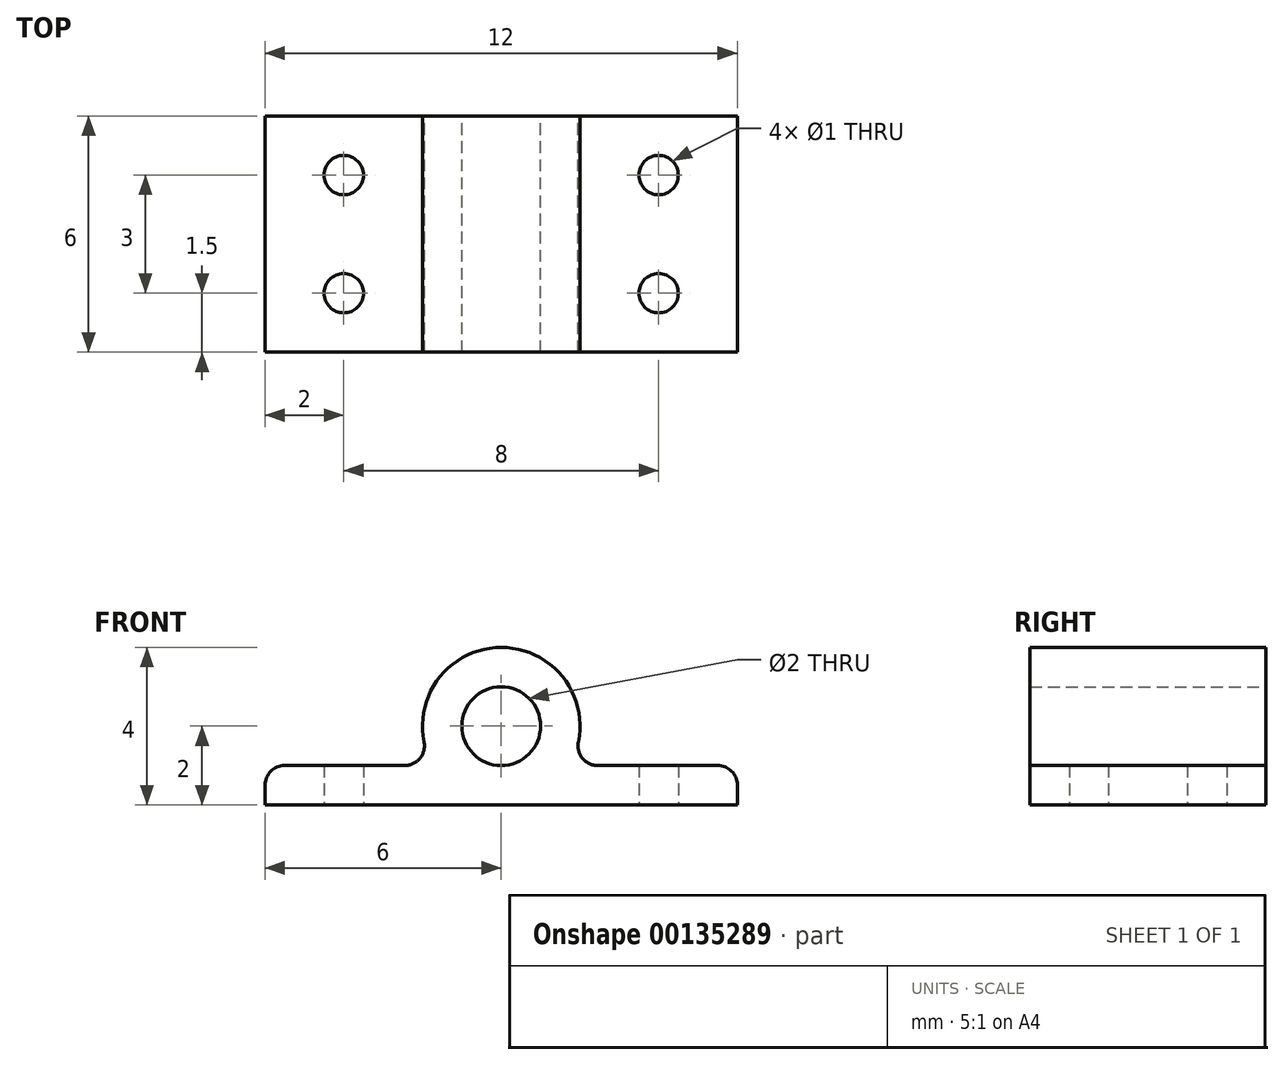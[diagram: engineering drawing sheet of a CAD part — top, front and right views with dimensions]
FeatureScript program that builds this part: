
annotation { "Feature Type Name" : "Feature", "Feature Type Description" : "" }
export const myFeature = defineFeature(function(context is Context, id is Id, definition is map)
    precondition{}
    {
        {
            var Q0;
            Q0=qCreatedBy(makeId("Front.planeOp"),FACE);
            var sketch = newSketch(context, id + "F0", { "sketchPlane" : qUnion([Q0])});
            skLineSegment(sketch, "E0.bottom", {"start": v(-6, 0.5) * mm, "end": v(-2.45, 0.5) * mm});
            skLineSegment(sketch, "E0.top", {"start": v(-6, -0.5) * mm, "end": v(6, -0.5) * mm});
            skLineSegment(sketch, "E0.left", {"start": v(-6, 0.5) * mm, "end": v(-6, -0.5) * mm});
            skLineSegment(sketch, "E0.right", {"start": v(6, 0.5) * mm, "end": v(6, -0.5) * mm});
            skPoint(sketch, "E0.middle", {"position": v(0, 0) * mm});
            skLineSegment(sketch, "E1", {"start": v(0, -0.5) * mm, "end": v(0, 1.5) * mm, "construction": true});
            skPoint(sketch, "E1.endSnap0", {"position": v(0, 0.5) * mm});
            skArc(sketch, "E2", {"start": v(1.96, 1.1) * mm, "mid": v(0, 3.5) * mm, "end": v(-1.96, 1.1) * mm});
            skLineSegment(sketch, "E3.trimOffspring", {"start": v(2.45, 0.5) * mm, "end": v(6, 0.5) * mm});
            skCircle(sketch, "E4", {"center": v(0, 1.5) * mm, "radius": 1 * mm});
            skPoint(sketch, "E5.visualSharp", {"position": v(1.73, 0.5) * mm});
            skArc(sketch, "E5.filletArc", {"start": v(1.96, 1.1) * mm, "mid": v(2.06, 0.68) * mm, "end": v(2.45, 0.5) * mm});
            skPoint(sketch, "E6.visualSharp", {"position": v(-1.73, 0.5) * mm});
            skArc(sketch, "E6.filletArc", {"start": v(-2.45, 0.5) * mm, "mid": v(-2.06, 0.68) * mm, "end": v(-1.96, 1.1) * mm});
            skSolve(sketch);
        }
        {
            var Q0;
            Q0 = qSketchRegion(id + "F0", true);
            extrude(context, id + "F1", {"entities" : qUnion([Q0]), "depth" : 6 * mm});
        }
        {
            var Q0;
            Q0=makeQuery(id+"F1.opExtrude","SWEPT_FACE",FACE,{"disambiguationData":[OSD([sQuery(id+"F0.wireOp",EDGE,"E0.top")])]});
            var sketch = newSketch(context, id + "F2", { "sketchPlane" : qUnion([Q0])});
            skCircle(sketch, "E7", {"center": v(-4, 4.5) * mm, "radius": 0.5 * mm});
            skCircle(sketch, "E8", {"center": v(4, 1.5) * mm, "radius": 0.5 * mm});
            skCircle(sketch, "E9", {"center": v(-4, 1.5) * mm, "radius": 0.5 * mm});
            skCircle(sketch, "E10", {"center": v(4, 4.5) * mm, "radius": 0.5 * mm});
            skLineSegment(sketch, "E11", {"start": v(4, -1.82) * mm, "end": v(4, 7.48) * mm, "construction": true});
            skLineSegment(sketch, "E12", {"start": v(-4, 6.94) * mm, "end": v(-4, -3.75) * mm, "construction": true});
            skLineSegment(sketch, "E13", {"start": v(-7.75, 4.5) * mm, "end": v(8, 4.5) * mm});
            skLineSegment(sketch, "E14", {"start": v(7.73, 1.5) * mm, "end": v(-8.17, 1.5) * mm, "construction": true});
            skSolve(sketch);
        }
        {
            var Q0;
            Q0 = qSketchRegion(id + "F2", true);
            extrude(context, id + "F3", {"entities" : qUnion([Q0]), "operationType" : NewBodyOperationType.REMOVE, "endBound" : BoundingType.THROUGH_ALL, "oppositeDirection" : true, "depth" : 25 * mm});
        }
        {
            var Q0;
            Q0=makeQuery(id+"F1.opExtrude","SWEPT_EDGE",EDGE,{"disambiguationData":[OSD([sQuery(id+"F0.wireOp",EDGE,"E0.bottom"),sQuery(id+"F0.wireOp",EDGE,"E0.left")])]});
            var Q1;
            Q1=makeQuery(id+"F1.opExtrude","SWEPT_EDGE",EDGE,{"disambiguationData":[OSD([sQuery(id+"F0.wireOp",EDGE,"E0.right"),sQuery(id+"F0.wireOp",EDGE,"E3.trimOffspring")])]});
            fillet(context, id + "F4", {"entities" : qUnion([Q0, Q1]), "radius" : 0.5 * mm, "tangentPropagation" : true, "allowEdgeOverflow" : false});
        }
    });
